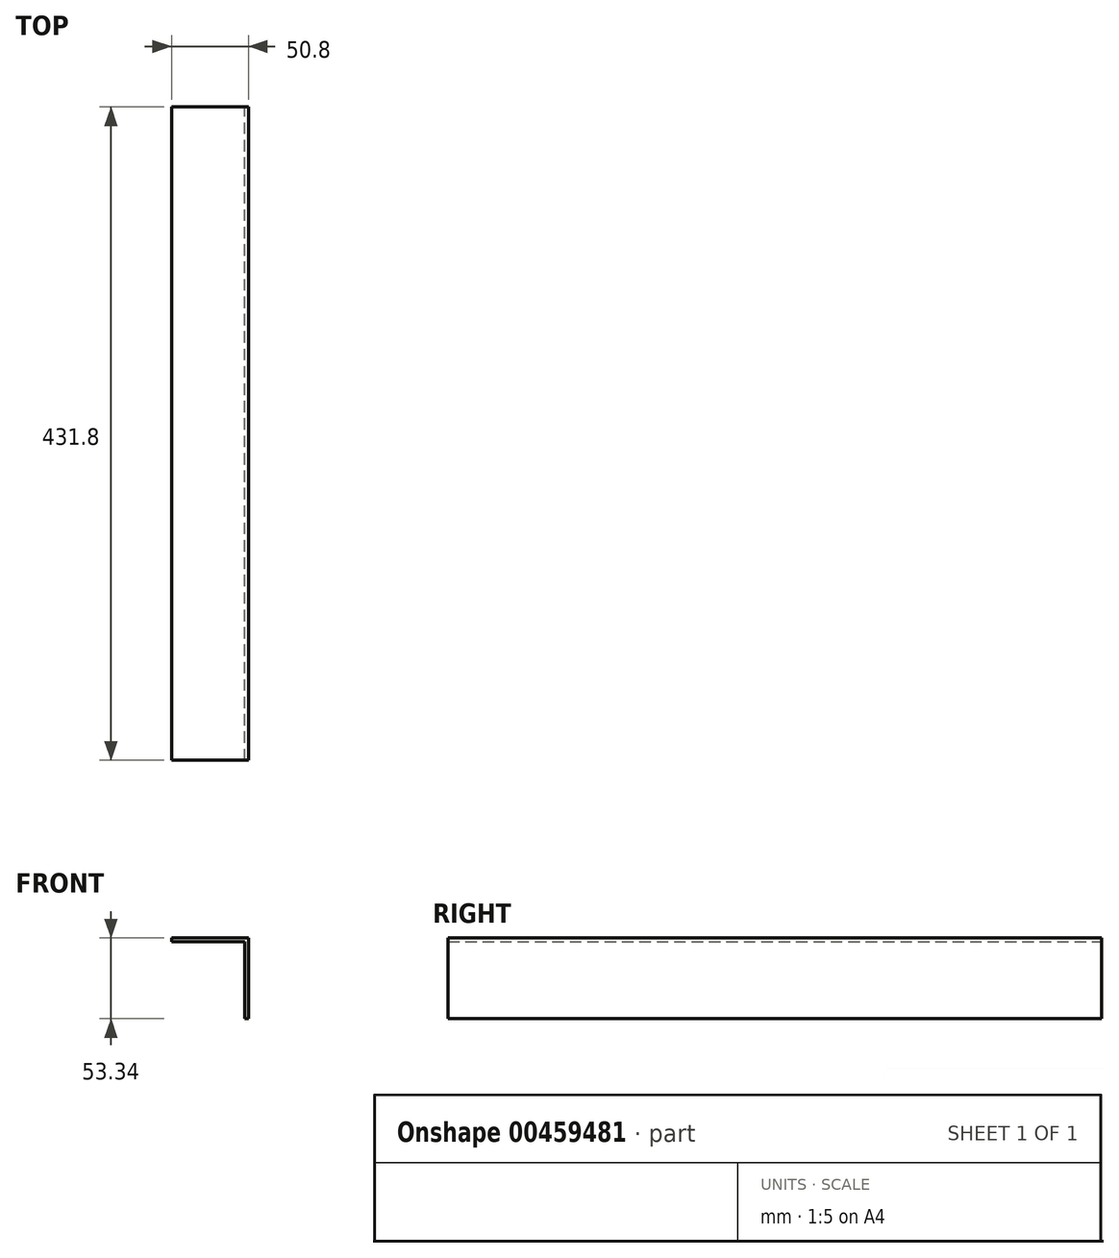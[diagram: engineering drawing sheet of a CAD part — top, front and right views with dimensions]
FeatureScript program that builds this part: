
annotation { "Feature Type Name" : "Feature", "Feature Type Description" : "" }
export const myFeature = defineFeature(function(context is Context, id is Id, definition is map)
    precondition{}
    {
        {
            var Q0;
            Q0=qCreatedBy(makeId("Top.planeOp"),FACE);
            var sketch = newSketch(context, id + "F0", { "sketchPlane" : qUnion([Q0])});
            skLineSegment(sketch, "E0", {"start": v(-19.21, -163.83) * mm, "end": v(-19.21, 267.97) * mm});
            skLineSegment(sketch, "E1", {"start": v(-19.21, 267.97) * mm, "end": v(31.59, 267.97) * mm});
            skLineSegment(sketch, "E2", {"start": v(31.59, 267.97) * mm, "end": v(31.59, -163.83) * mm});
            skLineSegment(sketch, "E3", {"start": v(31.59, -163.83) * mm, "end": v(-19.21, -163.83) * mm});
            skSolve(sketch);
        }
        {
            var Q0;
            Q0=makeQuery(id+"F0.imprint","IMPRINT",FACE,{"disambiguationData":[TD([[makeQuery(id+"F0.imprint","IMPRINT",EDGE,{"derivedFrom":sQuery(id+"F0.wireOp",EDGE,"E0")}),-1.0]])]});
            extrude(context, id + "F1", {"entities" : qUnion([Q0]), "depth" : 2.54 * mm});
        }
        {
            var Q0;
            Q0=makeQuery(id+"F1.opExtrude","CAP_FACE",FACE,{"disambiguationData":[OSD([sQuery(id+"F0.wireOp",EDGE,"E0"),sQuery(id+"F0.wireOp",EDGE,"E1"),sQuery(id+"F0.wireOp",EDGE,"E2"),sQuery(id+"F0.wireOp",EDGE,"E3")])],"isStart":true});
            var sketch = newSketch(context, id + "F2", { "sketchPlane" : qUnion([Q0])});
            skLineSegment(sketch, "E4", {"start": v(31.59, 163.83) * mm, "end": v(29.05, 163.83) * mm});
            skLineSegment(sketch, "E5", {"start": v(29.05, 163.83) * mm, "end": v(29.05, -267.97) * mm});
            skLineSegment(sketch, "E6", {"start": v(29.05, -267.97) * mm, "end": v(31.59, -267.97) * mm});
            skLineSegment(sketch, "E7", {"start": v(31.59, -267.97) * mm, "end": v(31.59, 163.83) * mm});
            skSolve(sketch);
        }
        {
            var Q0;
            Q0=makeQuery(id+"F2.imprint","IMPRINT",FACE,{"disambiguationData":[TD([[makeQuery(id+"F2.imprint","IMPRINT",EDGE,{"derivedFrom":sQuery(id+"F2.wireOp",EDGE,"E4")}),1.0]])]});
            extrude(context, id + "F3", {"entities" : qUnion([Q0]), "operationType" : NewBodyOperationType.ADD, "depth" : 50.8 * mm});
        }
    });
